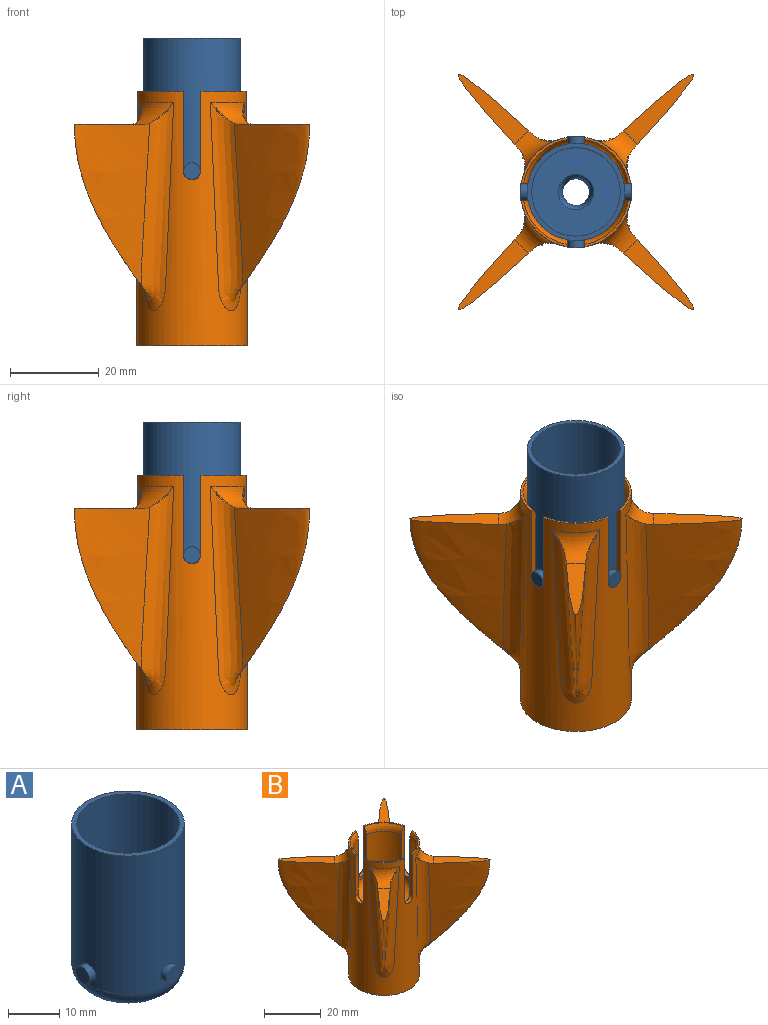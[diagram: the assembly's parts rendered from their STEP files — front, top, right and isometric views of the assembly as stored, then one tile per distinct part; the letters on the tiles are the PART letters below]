
ASSEMBLY  parts=2 mates=1
PART A: 15 faces, bbox 25x25x40.6 mm
  f0: cylinder r=11mm len=33mm, axis (0,0,-1), area 2235.1mm2, adj f1,f4,f5,f8,f9,f11
  f1: plane 22x22mm, normal (0,0,1), area 66mm2, adj f0,f12
  f2: plane 14x14mm, normal (0,0,-1), area 125.7mm2, adj f11,f14
  f3: plane 3.8x3.8mm, normal (0,1,0), area 11.3mm2, adj f4
  f4: cylinder r=1.9mm len=3.8mm, axis (0,1,0), area 18.9mm2, adj f0,f3
  f5: cylinder r=1.9mm len=3.8mm, axis (0,1,0), area 18.9mm2, adj f0,f6
  f6: plane 3.8x3.8mm, normal (0,-1,0), area 11.3mm2, adj f5
  f7: plane 3.8x3.8mm, normal (1,0,0), area 11.3mm2, adj f8
  f8: cylinder r=1.9mm len=3.8mm, axis (-1,0,0), area 18.9mm2, adj f0,f7
  f9: cylinder r=1.9mm len=3.8mm, axis (-1,0,0), area 18.9mm2, adj f0,f10
  f10: plane 3.8x3.8mm, normal (-1,0,0), area 11.3mm2, adj f9
  f11: torus R=7mm, axis (0,0,1), area 376.9mm2, adj f0,f2
  f12: cylinder r=10mm len=34mm, axis (0,0,1), area 2136.3mm2, adj f1,f13
  f13: plane 20x20mm, normal (0,0,1), area 263.9mm2, adj f12,f14
  f14: torus R=8mm, axis (0,0,1), area 67.5mm2, adj f2,f13
PART B: 45 faces, bbox 53.5x53.5x60.3 mm
  f0: plane 23x23mm, normal (0,0,-1), area 365.2mm2, adj f26,f27
  f1: cylinder r=12.5mm len=57.5mm, axis (0,0,-1), area 2547mm2, adj f4,f5,f6,f7,f8,f9,f10,f11
  f2: cylinder r=11mm len=22mm, axis (0,0,-1), area 977.5mm2, adj f4,f5,f7,f8,f10,f11,f13,f14
  f3: plane 14x14mm, normal (0,0,1), area 125.7mm2, adj f20,f25
  f4: plane 18.08x1.6mm, normal (1,0,0), area 26.4mm2, adj f1,f2,f6,f18,f23
  f5: plane 18.08x1.6mm, normal (0,-1,0), area 26.4mm2, adj f1,f2,f6,f19,f23
  f6: plane 10.34x10.34mm, normal (0,0,1), area 7.6mm2, adj f1,f4,f5,f23
  f7: plane 18.08x1.6mm, normal (0,1,0), area 26.4mm2, adj f1,f2,f9,f19,f22
  f8: plane 18.08x1.6mm, normal (1,0,0), area 26.4mm2, adj f1,f2,f9,f16,f22
  f9: plane 10.34x10.34mm, normal (0,0,1), area 7.6mm2, adj f1,f7,f8,f22
  f10: plane 18.08x1.6mm, normal (0,-1,0), area 26.4mm2, adj f1,f2,f12,f17,f24
  f11: plane 18.08x1.6mm, normal (-1,0,0), area 26.4mm2, adj f1,f2,f12,f18,f24
  f12: plane 10.34x10.34mm, normal (0,0,1), area 7.6mm2, adj f1,f10,f11,f24
  f13: plane 18.08x1.6mm, normal (-1,0,0), area 26.4mm2, adj f1,f2,f15,f16,f21
  f14: plane 18.08x1.6mm, normal (0,1,0), area 26.4mm2, adj f1,f2,f15,f17,f21
  f15: plane 10.34x10.34mm, normal (0,0,1), area 7.6mm2, adj f1,f13,f14,f21
  f16: cylinder r=2mm len=4mm, axis (0,-1,0), area 9.5mm2, adj f1,f2,f8,f13
  f17: cylinder r=2mm len=4mm, axis (-1,0,0), area 9.5mm2, adj f1,f2,f10,f14
  f18: cylinder r=2mm len=4mm, axis (0,-1,0), area 9.5mm2, adj f1,f2,f4,f11
  f19: cylinder r=2mm len=4mm, axis (-1,0,0), area 9.5mm2, adj f1,f2,f5,f7
  f20: torus R=7mm, axis (0,0,1), area 376.9mm2, adj f2,f3
  f21: torus R=16mm, axis (0,0,1), area 44.5mm2, adj f2,f13,f14,f15
  f22: torus R=16mm, axis (0,0,1), area 44.5mm2, adj f2,f7,f8,f9
  f23: torus R=16mm, axis (0,0,1), area 44.5mm2, adj f2,f4,f5,f6
  f24: torus R=16mm, axis (0,0,1), area 44.5mm2, adj f2,f10,f11,f12
  f25: cylinder r=3mm len=6mm, axis (0,0,1), area 1mm2, adj f3,f26
  f26: torus R=6.5mm, axis (0,0,-1), area 56.9mm2, adj f0,f25
  f27: cylinder r=11.5mm len=30mm, axis (0,0,-1), area 2167.7mm2, adj f0,f28
  f28: plane 25x25mm, normal (0,0,-1), area 75.4mm2, adj f1,f27
  f29: bspline ~40.57x19.71mm, area 1025.5mm2, adj f30,f40,f44
  f30: plane 15.96x15.96mm, normal (0,0,1), area 63.3mm2, adj f29,f44
  f31: bspline ~40.57x19.71mm, area 1025.5mm2, adj f32,f39,f43
  f32: plane 15.96x15.96mm, normal (0,0,1), area 63.3mm2, adj f31,f43
  f33: bspline ~40.57x19.71mm, area 1025.5mm2, adj f34,f38,f42
  f34: plane 15.96x15.96mm, normal (0,0,1), area 63.3mm2, adj f33,f42
  f35: bspline ~40.57x19.71mm, area 1025.5mm2, adj f36,f37,f41
  f36: plane 15.96x15.96mm, normal (0,0,1), area 63.3mm2, adj f35,f41
  f37: bspline ~52.29x9.01mm, area 492.4mm2, adj f1,f35,f41
  f38: bspline ~52.29x9.01mm, area 492.4mm2, adj f1,f33,f42
  f39: bspline ~52.29x9.01mm, area 492.4mm2, adj f1,f31,f43
  f40: bspline ~52.29x9.01mm, area 492.4mm2, adj f1,f29,f44
  f41: torus R=17.5mm, axis (0,0,1), area 56.8mm2, adj f1,f35,f36,f37
  f42: torus R=17.5mm, axis (0,0,1), area 56.8mm2, adj f1,f33,f34,f38
  f43: torus R=17.5mm, axis (0,0,1), area 56.8mm2, adj f1,f31,f32,f39
  f44: torus R=17.5mm, axis (0,0,1), area 56.8mm2, adj f1,f29,f30,f40
PLACE A t=(0,0,9.47)mm
PLACE B at identity
MATE slider A.f0 <-> B.f1  axis (0,0,-1) through (0,0,22.98)mm
